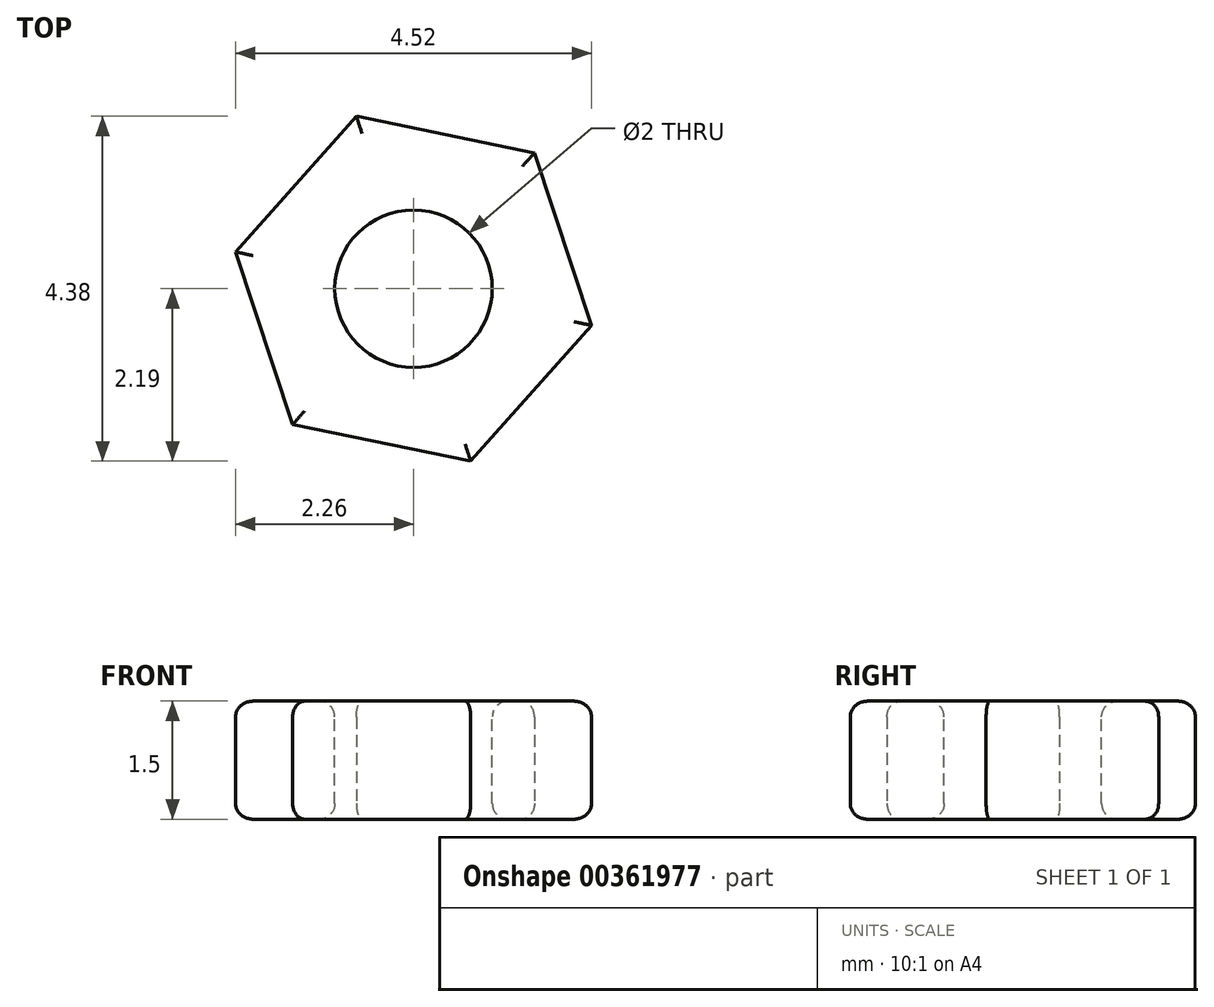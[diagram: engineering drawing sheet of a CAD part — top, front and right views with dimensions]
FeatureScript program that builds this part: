
annotation { "Feature Type Name" : "Feature", "Feature Type Description" : "" }
export const myFeature = defineFeature(function(context is Context, id is Id, definition is map)
    precondition{}
    {
        {
            var Q0;
            Q0=qCreatedBy(makeId("Top.planeOp"),FACE);
            var sketch = newSketch(context, id + "F0", { "sketchPlane" : qUnion([Q0])});
            skCircle(sketch, "E0.cCircle", {"center": v(0, 0) * mm, "radius": 2 * mm, "construction": true});
            skLineSegment(sketch, "E0.0", {"start": v(1.54, 1.73) * mm, "end": v(2.26, -0.47) * mm});
            skLineSegment(sketch, "E0.1", {"start": v(2.26, -0.47) * mm, "end": v(0.73, -2.2) * mm});
            skLineSegment(sketch, "E0.2", {"start": v(0.73, -2.2) * mm, "end": v(-1.54, -1.73) * mm});
            skLineSegment(sketch, "E0.3", {"start": v(-1.54, -1.73) * mm, "end": v(-2.26, 0.47) * mm});
            skLineSegment(sketch, "E0.4", {"start": v(-2.26, 0.47) * mm, "end": v(-0.73, 2.2) * mm});
            skLineSegment(sketch, "E0.5", {"start": v(-0.73, 2.2) * mm, "end": v(1.54, 1.73) * mm});
            skPoint(sketch, "E0.0.midPoint", {"position": v(1.9, 0.63) * mm});
            skSolve(sketch);
        }
        {
            var Q0;
            Q0=makeQuery(id+"F0.imprint","IMPRINT",FACE,{"disambiguationData":[TD([[makeQuery(id+"F0.imprint","IMPRINT",EDGE,{"derivedFrom":sQuery(id+"F0.wireOp",EDGE,"E0.0")}),-1.0]])]});
            extrude(context, id + "F1", {"entities" : qUnion([Q0]), "depth" : 1.5 * mm});
        }
        {
            var Q0;
            Q0=makeQuery(id+"F1.opExtrude","CAP_FACE",FACE,{"disambiguationData":[OSD([sQuery(id+"F0.wireOp",EDGE,"E0.0"),sQuery(id+"F0.wireOp",EDGE,"E0.1"),sQuery(id+"F0.wireOp",EDGE,"E0.2"),sQuery(id+"F0.wireOp",EDGE,"E0.3"),sQuery(id+"F0.wireOp",EDGE,"E0.4"),sQuery(id+"F0.wireOp",EDGE,"E0.5")])],"isStart":false});
            var sketch = newSketch(context, id + "F2", { "sketchPlane" : qUnion([Q0])});
            skCircle(sketch, "E1", {"center": v(0, 0) * mm, "radius": 1 * mm});
            skSolve(sketch);
        }
        {
            var Q0;
            Q0=makeQuery(id+"F2.imprint","IMPRINT",FACE,{"disambiguationData":[TD([[makeQuery(id+"F2.imprint","IMPRINT",EDGE,{"derivedFrom":sQuery(id+"F2.wireOp",EDGE,"E1")}),1.0]])]});
            extrude(context, id + "F3", {"entities" : qUnion([Q0]), "operationType" : NewBodyOperationType.REMOVE, "oppositeDirection" : true, "depth" : 25 * mm});
        }
        {
            var Q0;
            Q0=makeQuery(id+"F3.boolean.opBoolean","COPY",EDGE,{"derivedFrom":makeQuery(id+"F3.opExtrude","CAP_EDGE",EDGE,{"disambiguationData":[OSD([sQuery(id+"F2.wireOp",EDGE,"E1")])],"isStart":true})});
            var Q1;
            Q1=makeQuery(id+"F1.opExtrude","CAP_FACE",FACE,{"disambiguationData":[OSD([sQuery(id+"F0.wireOp",EDGE,"E0.0"),sQuery(id+"F0.wireOp",EDGE,"E0.1"),sQuery(id+"F0.wireOp",EDGE,"E0.2"),sQuery(id+"F0.wireOp",EDGE,"E0.3"),sQuery(id+"F0.wireOp",EDGE,"E0.4"),sQuery(id+"F0.wireOp",EDGE,"E0.5")])],"isStart":false});
            var Q2;
            Q2=makeQuery(id+"F1.opExtrude","CAP_FACE",FACE,{"disambiguationData":[OSD([sQuery(id+"F0.wireOp",EDGE,"E0.0"),sQuery(id+"F0.wireOp",EDGE,"E0.1"),sQuery(id+"F0.wireOp",EDGE,"E0.2"),sQuery(id+"F0.wireOp",EDGE,"E0.3"),sQuery(id+"F0.wireOp",EDGE,"E0.4"),sQuery(id+"F0.wireOp",EDGE,"E0.5")])],"isStart":true});
            fillet(context, id + "F4", {"entities" : qUnion([Q0, Q1, Q2]), "radius" : .2 * mm, "tangentPropagation" : true, "allowEdgeOverflow" : false});
        }
    });
